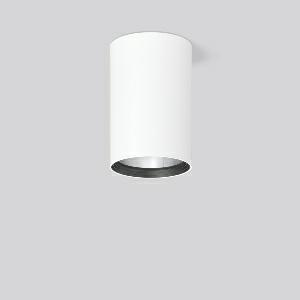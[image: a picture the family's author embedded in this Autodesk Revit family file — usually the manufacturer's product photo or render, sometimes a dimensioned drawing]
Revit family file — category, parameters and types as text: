
# Revit family: heledon_maxi_a_931218_002_2_de71
name_source: partatom
category: Lighting Fixtures
units: mm (PartAtom-declared; Revit-internal decimal feet)

## family parameters
Cut with Voids When Loaded = No
Host = Face
Light Source = No
Part Type = Normal
Room Calculation Point = No
Round Connector Dimension = Use Diameter
Shared = No

## types (1)
- HELEDON maxi A (1 x LED Modul 927, 3150 lm, 2700)
    Apparent Load = 25 VA
    Approval mark = CE
    CIE Flux Codes = 100 100 100 100 100
    Color Rendering = 92
    Color Temperature = 2700
    Default Elevation = 1800 mm
    Description = Series: HELEDON maxi
Cylindrical surface-mounted downlight. Housing: die-cast aluminium, powder-coated. Internal ceiling frame polycarbonate with bayonet mounting. Black plastic ring and recessed LED to prevent glare from the side. Optical assembly with reflector made of MIRO-Silver with 98% total light reflection for outstanding efficiency - can be changed without tools. Best colour rendering index Ra>90. Suitable for Ceiling mounting. Easy installation with a separate ceiling frame with bayonet mounting and plug connection. Driver integrated. Connected via plug-in connector. High quality converter without flickering and stroboscopic effect. The following accessories can be mounted without use of tools: interchangeable lenses, decorative glasses, honeycomb louvre, clear and frosted diffusers, white interchangeable plastic ring. 
Colour: traffic white, matt (RAL 9016)
Diameter: 123 mm
Height: 183 mm
Lamp: LED
Socket: without socket
Colour temperature: 2700K
Colour rendering index (CRI): 92
System power: 25 W
Rated luminous flux: 3150 lm
Luminous efficiency: 126 lm/W
Control gear: Regulated power supply
Protection class: I
Type of protection: IP 20
    Height = 183 mm
    Lamp = 1 x LED Modul 927
    Lamp Light Flux = 3150 lm
    Lamp count = 1
    Length = 123 mm
    Lifetime = 50000 h
    Luminous efficacy = 126 lm/W
    Manufacturer = RZB
    ModVariant = No
    Model = 931218.002.2
    Mounting Place = Ceiling
    Mounting Type = Surface mounted
    Number of Poles = 1
    OnlyDefault = Yes
    Power Factor = 1
    Product Name = HELEDON maxi A
    Product group = Surface mounted downlights
    ProductGroupID = 302
    Protection Class = Protection class I
    Protection Degree = IP 20
    RLX_Detail_Level = 1
    RLX_Emergency_Light_Flux = 0 lm
    RLX_Emergency_Type = 0
    RLX_Emergency_Type_DB = No
    RlxData = <blob elided: 97109 chars, md5=723975fa>
    Socket = socket
    Standby Power = 0 W
    System Light Flux = 3150 lm
    System Power = 25 W
    Type Comments = Product without accessories
    Type Image = 931192.002.jpg
    URL = http://relux.com
    VarID = ---
    Voltage = 230 V
    Voltage Range = 220-240 V
    Weight = 0.00 kg
    Width = 0 mm  [stored 0 ft]

note: [stored X ft] marks values corroborated as IEEE doubles in the binary element streams (Revit-internal decimal feet)

## geometry (parser evidence)
native form markers: Blend x4, Sweep x9
no freeform markers — native parametric forms only
